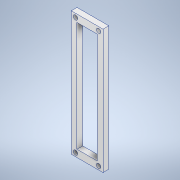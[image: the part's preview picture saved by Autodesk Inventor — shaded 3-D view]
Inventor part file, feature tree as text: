
AUTODESK INVENTOR PART (.ipt)
format: ipt  version: 2020 (Build 240168000, 168)  size: 126,464 bytes
history: native  units: mm
features: extrude x1, sketch x1
ambient origin geometry x8: Origin, YZ Plane, XZ Plane, XY Plane, X Axis, Y Axis, Z Axis, Center Point
bodies: Solid1 (feature_tree)
feature tree (2):
  extrude  "Extrusion1"  Depth=86.0mm
  sketch  "Sketch1"  dims[d0=22.0mm d1=86.0mm d2=3.0mm d3=3.0mm d4=3.0mm d5=3.0mm d6=3.0mm d7=2.5mm d8=3.0mm d9=2.5mm d10=2.5mm d11=3.0mm d12=3.0mm d13=2.5mm d14=14.0mm d15=76.0mm d16=4.0mm d17=0.0mm]
